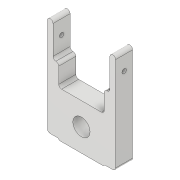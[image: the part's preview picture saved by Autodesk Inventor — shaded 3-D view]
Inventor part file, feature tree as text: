
AUTODESK INVENTOR PART (.ipt)
format: ipt  version: 2018.3 (Build 223284000, 284)  size: 179,200 bytes
history: native  units: in
note: dims shown in document units (in); Inventor stores cm internally (conversion verified against a paired STEP export)
features: extrude x7, fillet x7, sketch x7
ambient origin geometry x8: Origin, YZ Plane, XZ Plane, XY Plane, X Axis, Y Axis, Z Axis, Center Point
bodies: Solid1 (feature_tree)
feature tree (21):
  extrude  "Extrusion1"  Depth=2.0in
  fillet  "Fillet1"  Radius=2.0in
  extrude  "Extrusion2"  Depth=0.0625in
  extrude  "Extrusion3"  Depth=2.5in TaperAngle=0.0deg
  extrude  "Extrusion4"  Depth=2.5in TaperAngle=0.0deg
  extrude  "Extrusion5"  Depth=0.125in
  fillet  "Fillet3"  Radius=4.0in
  extrude  "Extrusion7"  Depth=0.125in
  fillet  "Fillet7"  Radius=1.0in
  fillet  "Fillet9"  Radius=1.0in
  extrude  "Extrusion8"  Depth=0.125in TaperAngle=0.0deg
  fillet  "Fillet10"  Radius=0.125in
  fillet  "Fillet11"  Radius=0.125in
  fillet  "Fillet12"  Radius=0.125in
  sketch  "Sketch1"  dims[d0=0.755in d1=2.0in d2=2.0in]
  sketch  "Sketch2"  dims[d3=0.75in d4=0.0in d5=0.0625in]
  sketch  "Sketch3"  dims[d6=0.5in d7=0.0in d8=2.5in d9=0.0in]
  sketch  "Sketch4"  dims[d11=0.5in d12=0.0in d13=2.5in d14=0.0in]
  sketch  "Sketch5"  dims[d15=0.125in d20=0.1925in d21=4.0in d22=0.0in]
  sketch  "Sketch7"  dims[d33=0.0625in d35=0.125in d36=1.0in d37=1.0in]
  sketch  "Sketch8"  dims[d38=0.75in d39=1.5in d40=0.0in d41=0.125in d42=0.125in d43=0.125in d23=1.0in d24=1.0in]
